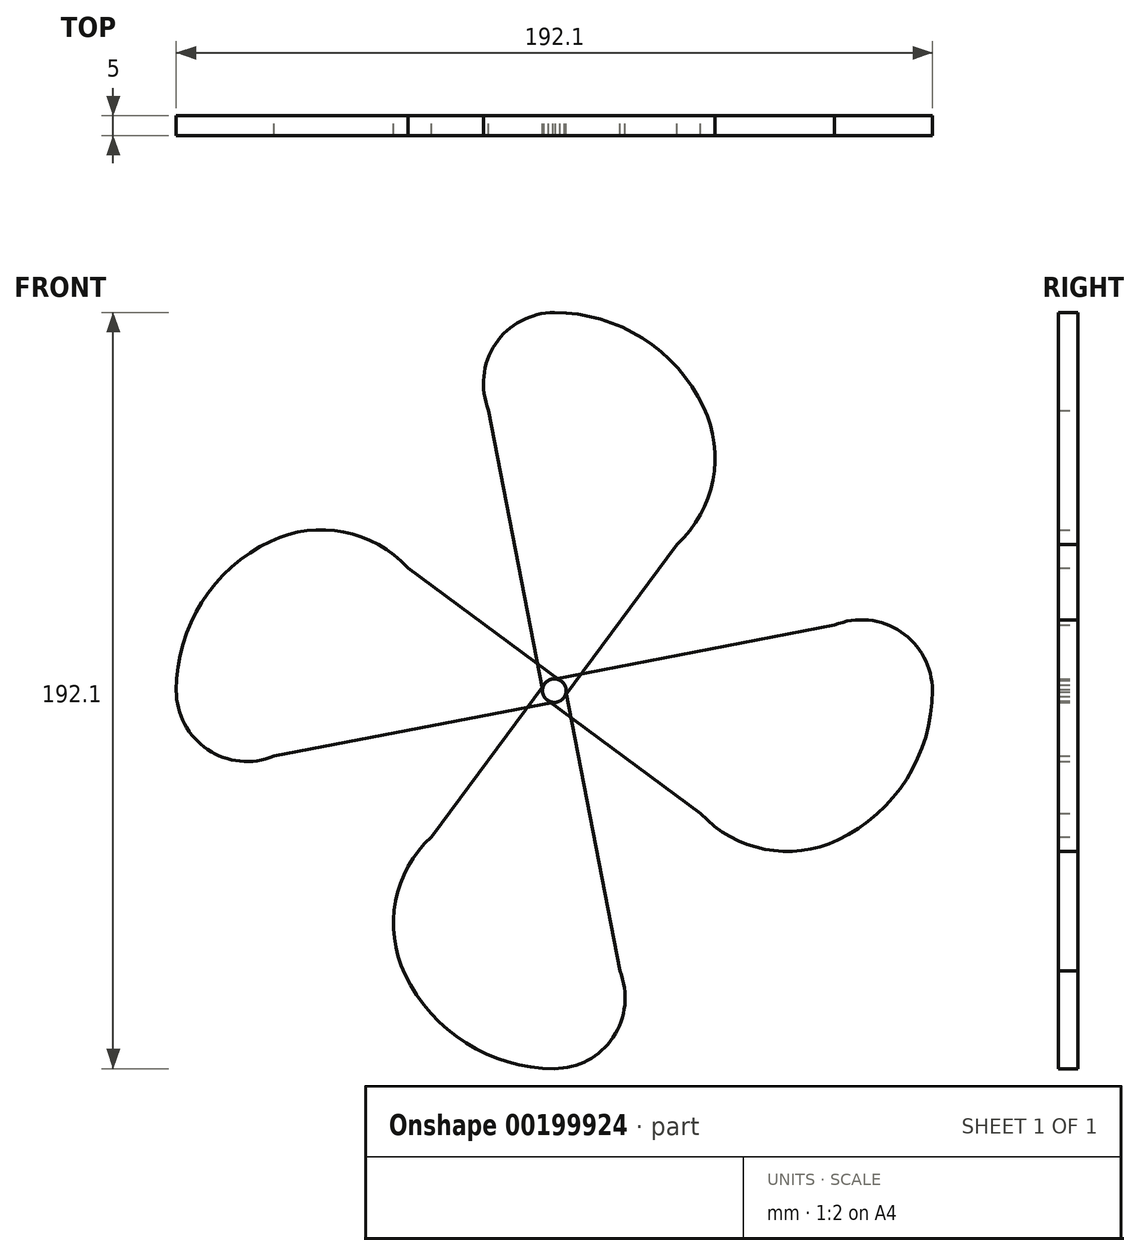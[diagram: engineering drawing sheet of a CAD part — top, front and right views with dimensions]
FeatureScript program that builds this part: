
annotation { "Feature Type Name" : "Feature", "Feature Type Description" : "" }
export const myFeature = defineFeature(function(context is Context, id is Id, definition is map)
    precondition{}
    {
        {
            var Q0;
            Q0=qCreatedBy(makeId("Front.planeOp"),FACE);
            var sketch = newSketch(context, id + "F0", { "sketchPlane" : qUnion([Q0])});
            skCircle(sketch, "E0", {"center": v(0, 0) * mm, "radius": 42 * mm});
            skCircle(sketch, "E1", {"center": v(0, 24) * mm, "radius": 18 * mm});
            skCircle(sketch, "E2", {"center": v(10.84, 5.15) * mm, "radius": 30 * mm});
            skCircle(sketch, "E3", {"center": v(0, -54.05) * mm, "radius": 12 * mm});
            skCircle(sketch, "E4", {"center": v(0, -54.05) * mm, "radius": 3 * mm});
            skLineSegment(sketch, "E5", {"start": v(-2.98, -53.73) * mm, "end": v(-16.65, 17.16) * mm});
            skLineSegment(sketch, "E6", {"start": v(2.14, -56.15) * mm, "end": v(31.19, -16.9) * mm});
            skSolve(sketch);
        }
        {
            var Q0;
            {var subQ0=sQuery(id+"F0.wireOp",EDGE,"E2");var subQ1=sQuery(id+"F0.wireOp",EDGE,"E1");var subQ3=makeQuery(id+"F0.imprint","INTERSECT",VERTEX,{"derivedFrom":[subQ1,subQ0]});Q0=makeQuery(id+"F0.imprint","IMPRINT",FACE,{"disambiguationData":[TD([[makeQuery(id+"F0.imprint","IMPRINT",EDGE,{"disambiguationData":[TD([[subQ3,1.0]])],"derivedFrom":subQ1}),1.0]])]});}
            var Q1;
            {var subQ0=sQuery(id+"F0.wireOp",EDGE,"E1");var subQ1=makeQuery(id+"F0.imprint","INTERSECT",VERTEX,{"derivedFrom":[sQuery(id+"F0.wireOp",EDGE,"E0"),subQ0]});Q1=makeQuery(id+"F0.imprint","IMPRINT",FACE,{"disambiguationData":[TD([[makeQuery(id+"F0.imprint","IMPRINT",EDGE,{"disambiguationData":[TD([[subQ1,1.0]])],"derivedFrom":subQ0}),1.0]])]});}
            var Q2;
            {var subQ0=sQuery(id+"F0.wireOp",EDGE,"E2");var subQ2=makeQuery(id+"F0.imprint","INTERSECT",VERTEX,{"derivedFrom":[sQuery(id+"F0.wireOp",EDGE,"E0"),subQ0]});Q2=makeQuery(id+"F0.imprint","IMPRINT",FACE,{"disambiguationData":[TD([[makeQuery(id+"F0.imprint","IMPRINT",EDGE,{"disambiguationData":[TD([[subQ2,-1.0]])],"derivedFrom":subQ0}),1.0]])]});}
            var Q3;
            {var subQ0=sQuery(id+"F0.wireOp",EDGE,"E5");var subQ1=sQuery(id+"F0.wireOp",EDGE,"E0");var subQ2=makeQuery(id+"F0.imprint","INTERSECT",VERTEX,{"derivedFrom":[subQ1,subQ0]});Q3=makeQuery(id+"F0.imprint","IMPRINT",FACE,{"disambiguationData":[TD([[makeQuery(id+"F0.imprint","IMPRINT",EDGE,{"disambiguationData":[TD([[subQ2,-1.0]])],"derivedFrom":subQ1}),1.0]])]});}
            var Q4;
            {var subQ0=sQuery(id+"F0.wireOp",EDGE,"E5");var subQ1=sQuery(id+"F0.wireOp",EDGE,"E0");var subQ2=makeQuery(id+"F0.imprint","INTERSECT",VERTEX,{"derivedFrom":[subQ1,subQ0]});Q4=makeQuery(id+"F0.imprint","IMPRINT",FACE,{"disambiguationData":[TD([[makeQuery(id+"F0.imprint","IMPRINT",EDGE,{"disambiguationData":[TD([[subQ2,-1.0]])],"derivedFrom":subQ1}),-1.0]])]});}
            var Q5;
            {var subQ0=sQuery(id+"F0.wireOp",EDGE,"E5");var subQ1=sQuery(id+"F0.wireOp",EDGE,"E3");var subQ2=makeQuery(id+"F0.imprint","INTERSECT",VERTEX,{"derivedFrom":[subQ1,subQ0]});Q5=makeQuery(id+"F0.imprint","IMPRINT",FACE,{"disambiguationData":[TD([[makeQuery(id+"F0.imprint","IMPRINT",EDGE,{"disambiguationData":[TD([[subQ2,1.0]])],"derivedFrom":subQ1}),1.0]])]});}
            var Q6;
            {var subQ0=sQuery(id+"F0.wireOp",EDGE,"E1");var subQ1=sQuery(id+"F0.wireOp",EDGE,"E0");var subQ2=makeQuery(id+"F0.imprint","INTERSECT",VERTEX,{"derivedFrom":[subQ1,subQ0]});Q6=makeQuery(id+"F0.imprint","IMPRINT",FACE,{"disambiguationData":[TD([[makeQuery(id+"F0.imprint","IMPRINT",EDGE,{"disambiguationData":[TD([[subQ2,1.0]])],"derivedFrom":subQ1}),1.0]])]});}
            extrude(context, id + "F1", {"entities" : qUnion([Q0, Q1, Q2, Q3, Q4, Q5, Q6]), "endBound" : BoundingType.SYMMETRIC, "depth" : 5 * mm});
        }
        {
            var Q0;
            Q0=makeQuery(id+"F1.opExtrude","SWEPT_BODY",BODY,{"disambiguationData":[OSD([sQuery(id+"F0.wireOp",EDGE,"E0"),sQuery(id+"F0.wireOp",EDGE,"E1"),sQuery(id+"F0.wireOp",EDGE,"E2"),sQuery(id+"F0.wireOp",EDGE,"E4"),sQuery(id+"F0.wireOp",EDGE,"E5"),sQuery(id+"F0.wireOp",EDGE,"E6")])]});
            var Q1;
            Q1=sQuery(id+"F0.wireOp",EDGE,"E4");
            circularPattern(context, id + "F2", {"entities" : qUnion([Q0]), "axis" : qUnion([Q1]), "angle" : 360 * degree, "instanceCount" : 4, "equalSpace" : true});
        }
    });
